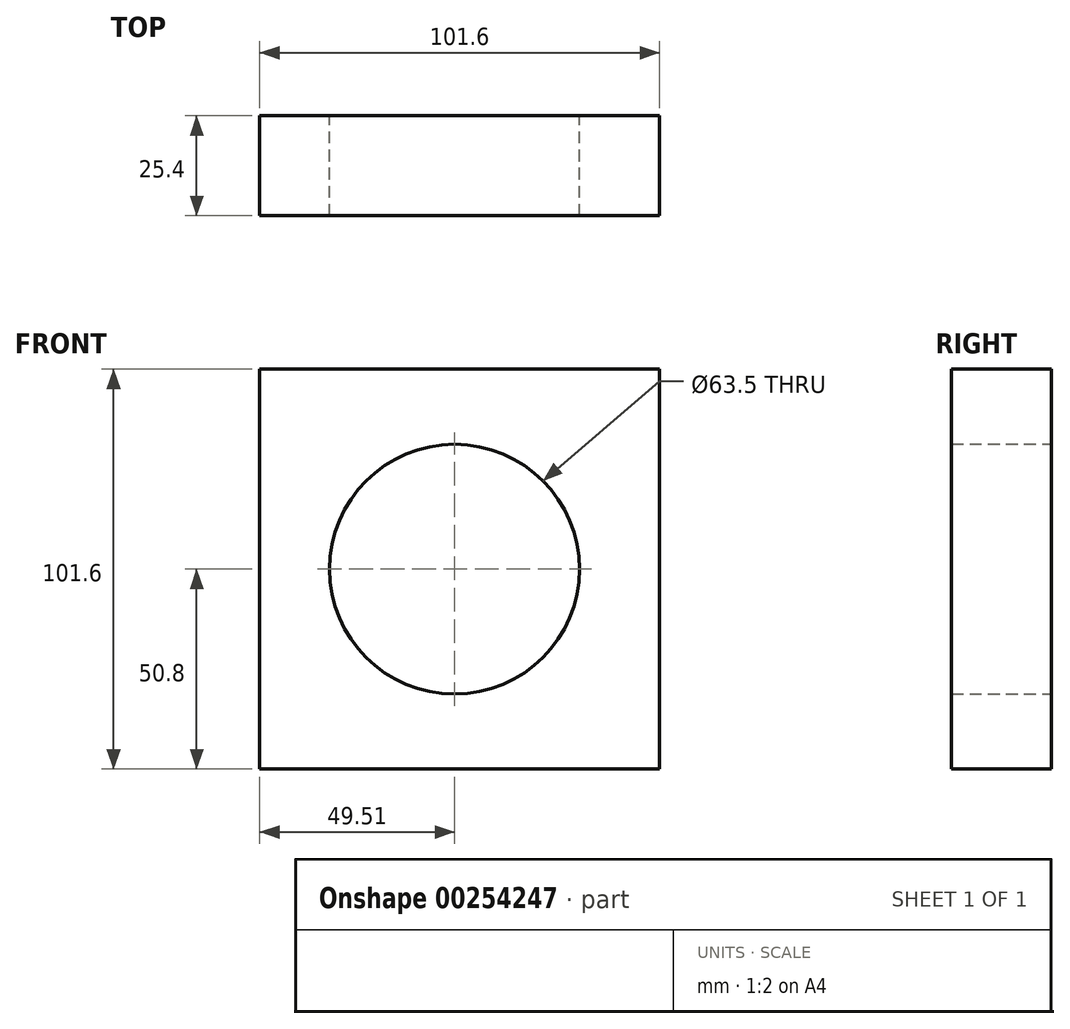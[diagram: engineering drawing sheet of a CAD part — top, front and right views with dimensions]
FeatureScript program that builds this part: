
annotation { "Feature Type Name" : "Feature", "Feature Type Description" : "" }
export const myFeature = defineFeature(function(context is Context, id is Id, definition is map)
    precondition{}
    {
        {
            var Q0;
            Q0=qCreatedBy(makeId("Front.planeOp"),FACE);
            var sketch = newSketch(context, id + "F0", { "sketchPlane" : qUnion([Q0])});
            skCircle(sketch, "E0", {"center": v(0, 0) * mm, "radius": 31.75 * mm});
            skLineSegment(sketch, "E1.bottom", {"start": v(52.1, -50.8) * mm, "end": v(-49.5, -50.8) * mm});
            skLineSegment(sketch, "E1.top", {"start": v(52.1, 50.8) * mm, "end": v(-49.5, 50.8) * mm});
            skLineSegment(sketch, "E1.left", {"start": v(52.1, -50.8) * mm, "end": v(52.1, 50.8) * mm});
            skLineSegment(sketch, "E1.right", {"start": v(-49.5, -50.8) * mm, "end": v(-49.5, 50.8) * mm});
            skPoint(sketch, "E1.middle", {"position": v(1.3, 0) * mm});
            skLineSegment(sketch, "E2.bottom", {"start": v(76.2, -76.2) * mm, "end": v(-76.2, -76.2) * mm});
            skLineSegment(sketch, "E2.top", {"start": v(76.2, 76.2) * mm, "end": v(-76.2, 76.2) * mm});
            skLineSegment(sketch, "E2.left", {"start": v(76.2, -76.2) * mm, "end": v(76.2, 76.2) * mm});
            skLineSegment(sketch, "E2.right", {"start": v(-76.2, -76.2) * mm, "end": v(-76.2, 76.2) * mm});
            skSolve(sketch);
        }
        {
            var Q0;
            Q0=makeQuery(id+"F0.imprint","IMPRINT",FACE,{"disambiguationData":[TD([[makeQuery(id+"F0.imprint","IMPRINT",EDGE,{"derivedFrom":sQuery(id+"F0.wireOp",EDGE,"E0")}),-1.0]])]});
            extrude(context, id + "F1", {"entities" : qUnion([Q0]), "depth" : 25.4 * mm});
        }
    });
